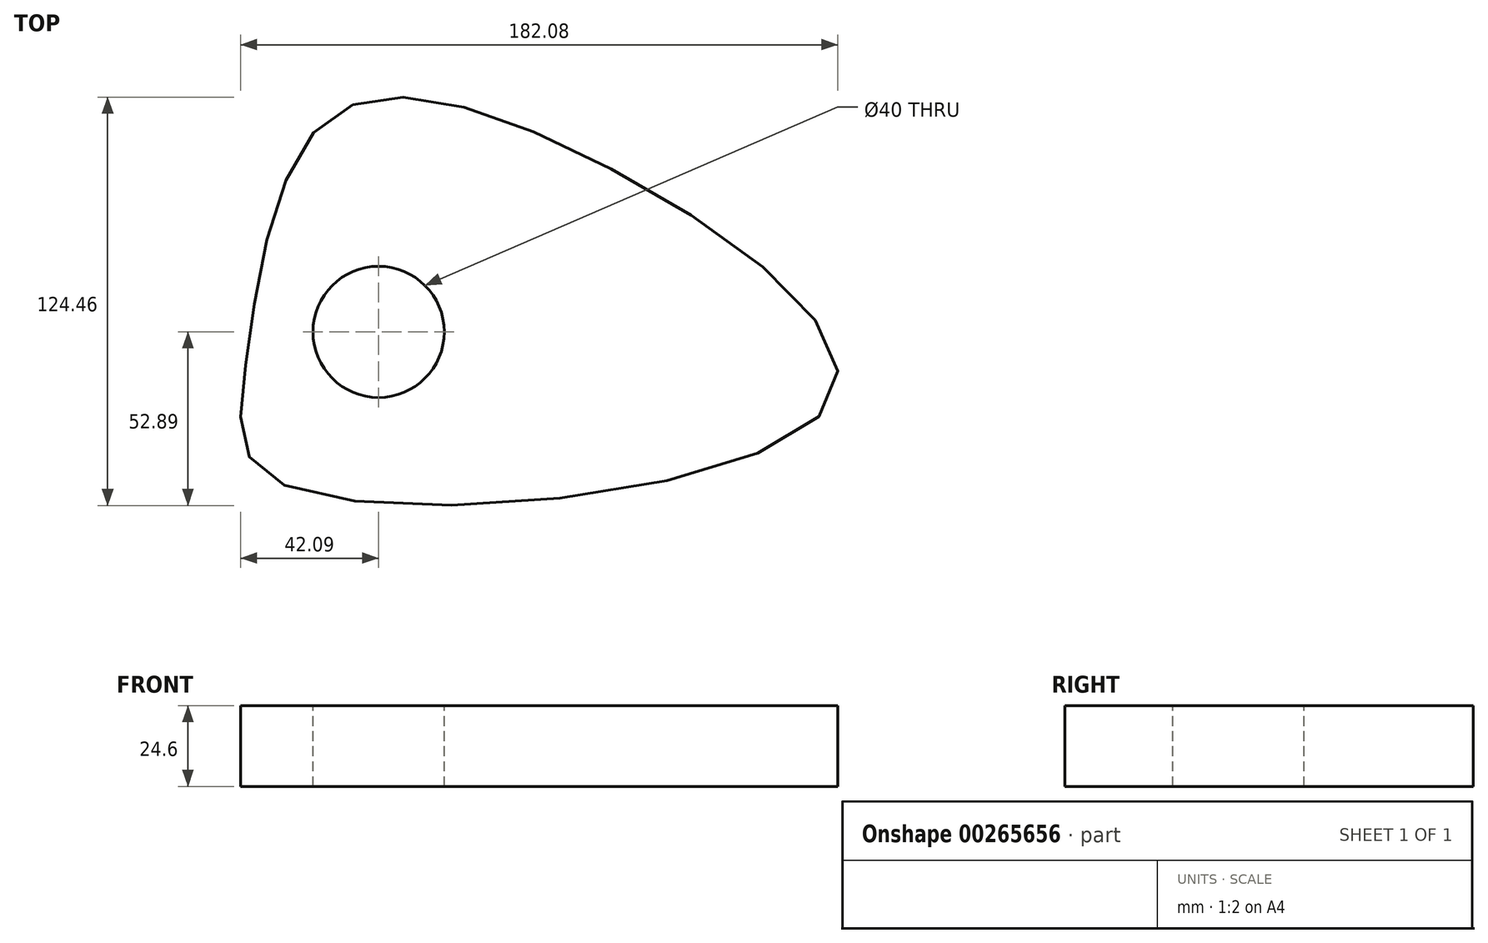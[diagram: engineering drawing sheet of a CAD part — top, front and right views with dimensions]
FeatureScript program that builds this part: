
annotation { "Feature Type Name" : "Feature", "Feature Type Description" : "" }
export const myFeature = defineFeature(function(context is Context, id is Id, definition is map)
    precondition{}
    {
        {
            var Q0;
            Q0=qCreatedBy(makeId("Top.planeOp"),FACE);
            var sketch = newSketch(context, id + "F0", { "sketchPlane" : qUnion([Q0])});
            skFitSpline(sketch, "E0", {"points": [v(-90.7, -44.22) * mm, v(-66.82, 29.81) * mm, v(11.3, 20.34) * mm, v(87.6, -55.37) * mm, v(-78.32, -81) * mm, v(-90.7, -44.22) * mm]});
            skSolve(sketch);
        }
        {
            var Q0;
            Q0=makeQuery(id+"F0.imprint","IMPRINT",FACE,{"disambiguationData":[TD([[makeQuery(id+"F0.imprint","IMPRINT",EDGE,{"derivedFrom":sQuery(id+"F0.wireOp",EDGE,"E0")}),-1.0]])]});
            extrude(context, id + "F1", {"entities" : qUnion([Q0]), "depth" : 24.6 * mm});
        }
        {
            var Q0;
            Q0=makeQuery(id+"F1.opExtrude","CAP_FACE",FACE,{"disambiguationData":[OSD([sQuery(id+"F0.wireOp",EDGE,"E0")])],"isStart":false});
            var sketch = newSketch(context, id + "F2", { "sketchPlane" : qUnion([Q0])});
            skPoint(sketch, "E1", {"position": v(-50.17, -34.06) * mm});
            skSolve(sketch);
        }
        {
            var Q0;
            Q0=sQuery(id+"F2.wireOp",VERTEX,"E1");
            var Q1;
            Q1=makeQuery(id+"F1.opExtrude","SWEPT_BODY",BODY,{"disambiguationData":[OSD([sQuery(id+"F0.wireOp",EDGE,"E0")])]});
            hole(context, id + "F3", {"style" : HoleStyle.SIMPLE, "endStyle" : HoleEndStyle.THROUGH, "holeDiameter" : 40 * mm, "tappedDepth" : 12 * mm, "tapClearance" : 3, "locations" : qUnion([Q0]), "scope" : qUnion([Q1])});
        }
        {
            var Q0;
            Q0=makeQuery(id+"F1.opExtrude","SWEPT_BODY",BODY,{"disambiguationData":[OSD([sQuery(id+"F0.wireOp",EDGE,"E0")])]});
            var Q1;
            Q1=sQuery(id+"F2.wireOp",VERTEX,"E1");
            var Q2;
            Q2=qCreatedBy(makeId("Origin.pointOp"),VERTEX);
            transform(context, id + "F4", {"entities" : qUnion([Q0]), "transformType" : TransformType.TRANSLATION_ENTITY, "oppositeDirectionEntity" : false, "transformLine" : qUnion([Q1, Q2]), "makeCopy" : false});
        }
    });
